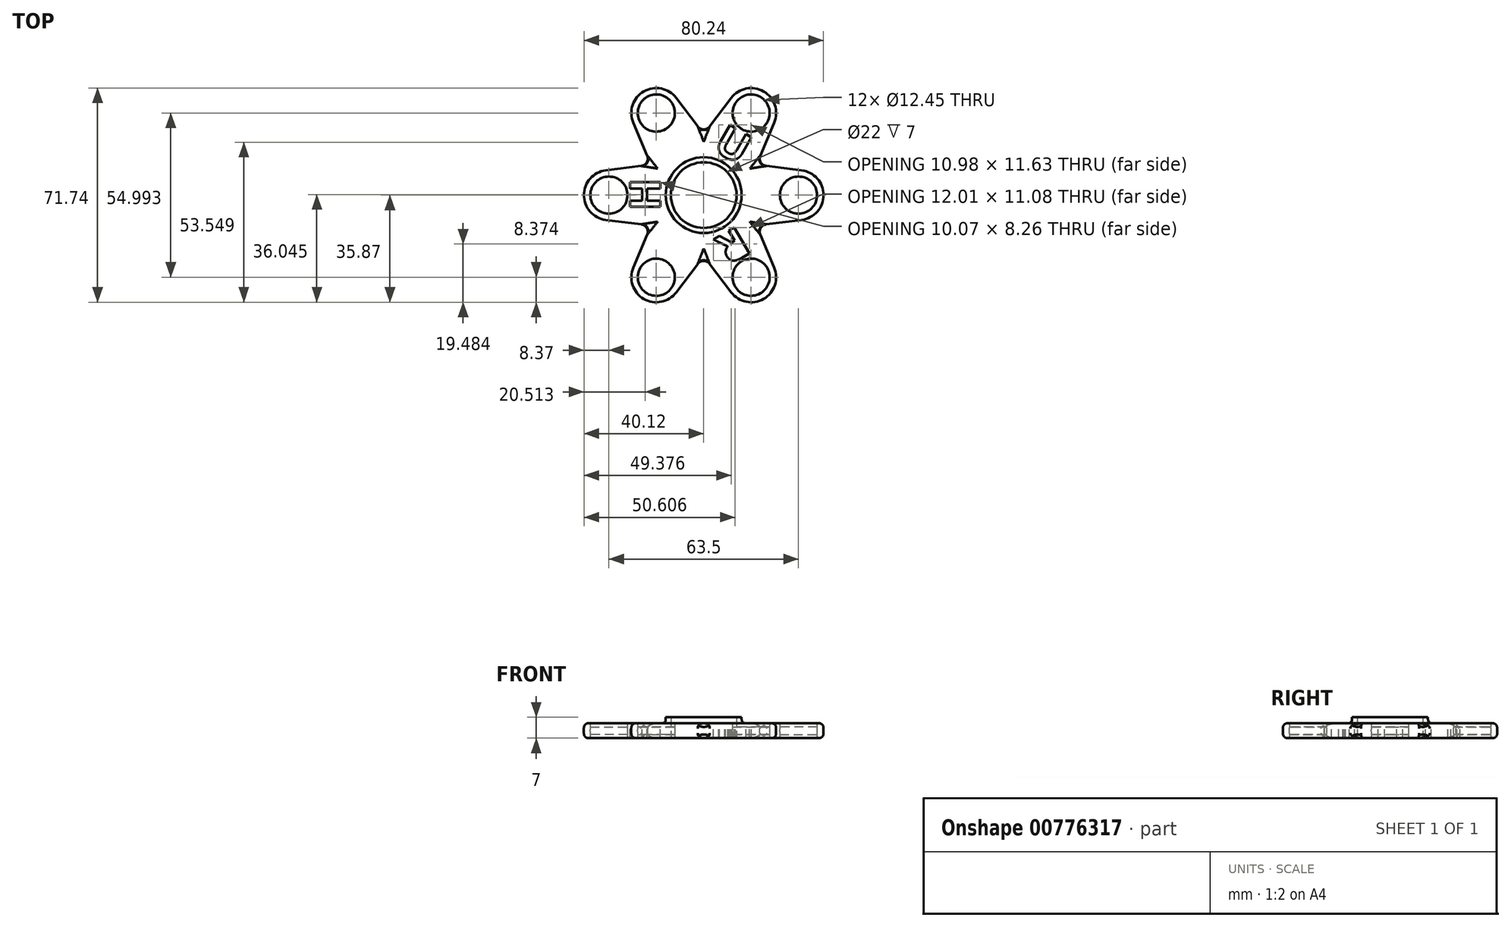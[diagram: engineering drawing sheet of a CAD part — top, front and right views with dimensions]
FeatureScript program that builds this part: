
annotation { "Feature Type Name" : "Feature", "Feature Type Description" : "" }
export const myFeature = defineFeature(function(context is Context, id is Id, definition is map)
    precondition{}
    {
        {
            var Q0;
            Q0=qCreatedBy(makeId("Top.planeOp"),FACE);
            var sketch = newSketch(context, id + "F0", { "sketchPlane" : qUnion([Q0])});
            skCircle(sketch, "E0", {"center": v(0, 0) * mm, "radius": 12.7 * mm});
            skCircle(sketch, "E1", {"center": v(0, 0) * mm, "radius": 11 * mm});
            skSolve(sketch);
        }
        {
            var Q0;
            Q0=makeQuery(id+"F0.imprint","IMPRINT",FACE,{"disambiguationData":[TD([[makeQuery(id+"F0.imprint","IMPRINT",EDGE,{"derivedFrom":sQuery(id+"F0.wireOp",EDGE,"E0")}),1.0]])]});
            extrude(context, id + "F1", {"entities" : qUnion([Q0]), "depth" : 7 * mm, "offsetDistance" : 25.4 * mm});
        }
        {
            var Q0;
            Q0=qCreatedBy(makeId("Top.planeOp"),FACE);
            cPlane(context, id + "F2", {"entities" : qUnion([Q0]), "cplaneType" : CPlaneType.OFFSET, "offset" : 2.5 * mm, "width" : 152.4 * mm, "height" : 152.4 * mm});
        }
        {
            var Q0;
            Q0=qCreatedBy(id+"F2.planeOp",FACE);
            var sketch = newSketch(context, id + "F3", { "sketchPlane" : qUnion([Q0])});
            skArc(sketch, "E2", {"start": v(-32.77, 8.31) * mm, "mid": v(-40.12, 0) * mm, "end": v(-32.77, -8.31) * mm});
            skLineSegment(sketch, "E3", {"start": v(-32.77, 8.31) * mm, "end": v(0, 12.35) * mm});
            skLineSegment(sketch, "E4.MirrorCS", {"start": v(-32.77, -8.31) * mm, "end": v(0, -12.35) * mm});
            skLineSegment(sketch, "E5", {"start": v(0, 12.35) * mm, "end": v(0, 11.32) * mm});
            skArc(sketch, "E6", {"start": v(0, 11.32) * mm, "mid": v(-11.32, 0) * mm, "end": v(0, -11.32) * mm});
            skLineSegment(sketch, "E7.trimOffspring", {"start": v(0, -11.32) * mm, "end": v(0, -12.35) * mm});
            skArc(sketch, "E8", {"start": v(-31.75, 6.35) * mm, "mid": v(-38.1, 0) * mm, "end": v(-31.75, -6.35) * mm});
            skLineSegment(sketch, "E9", {"start": v(-31.75, 6.35) * mm, "end": v(-31.75, -6.35) * mm});
            skCircle(sketch, "E10", {"center": v(-31.75, 0) * mm, "radius": 6.22 * mm});
            skSolve(sketch);
        }
        {
            var Q0;
            Q0=makeQuery(id+"F3.imprint","IMPRINT",FACE,{"disambiguationData":[TD([[makeQuery(id+"F3.imprint","IMPRINT",EDGE,{"derivedFrom":sQuery(id+"F3.wireOp",EDGE,"E2")}),1.0]])]});
            var Q1;
            {var subQ0=sQuery(id+"F3.wireOp",EDGE,"E8");Q1=makeQuery(id+"F3.imprint","IMPRINT",FACE,{"disambiguationData":[TD([[makeQuery(id+"F3.imprint","IMPRINT",EDGE,{"derivedFrom":subQ0}),1.0]])]});}
            extrude(context, id + "F4", {"entities" : qUnion([Q0, Q1]), "endBound" : BoundingType.SYMMETRIC, "depth" : 5 * mm, "offsetDistance" : 25.4 * mm});
        }
        {
            var Q0;
            Q0=qCreatedBy(makeId("Front.planeOp"),FACE);
            var sketch = newSketch(context, id + "F5", { "sketchPlane" : qUnion([Q0])});
            skLineSegment(sketch, "E11", {"start": v(0, 0) * mm, "end": v(0, 41) * mm, "construction": true});
            skSolve(sketch);
        }
        {
            var Q0;
            Q0=makeQuery(id+"F3.imprint","IMPRINT",FACE,{"disambiguationData":[TD([[makeQuery(id+"F3.imprint","IMPRINT",EDGE,{"derivedFrom":sQuery(id+"F3.wireOp",EDGE,"E8")}),1.0]])]});
            var Q1;
            Q1=sQuery(id+"F3.wireOp",EDGE,"E9");
            revolve(context, id + "F6", {"operationType" : NewBodyOperationType.REMOVE, "surfaceOperationType" : NewSurfaceOperationType.NEW, "entities" : qUnion([Q0]), "axis" : qUnion([Q1]), "revolveType" : RevolveType.FULL, "oppositeDirection" : true});
        }
        {
            var Q0;
            Q0=makeQuery(id+"F4.opExtrude","SWEPT_BODY",BODY,{"disambiguationData":[OSD([sQuery(id+"F3.wireOp",EDGE,"E2"),sQuery(id+"F3.wireOp",EDGE,"E3"),sQuery(id+"F3.wireOp",EDGE,"E4.MirrorCS"),sQuery(id+"F3.wireOp",EDGE,"E5"),sQuery(id+"F3.wireOp",EDGE,"gVdO0x3I-Yq7t-95zV-3Q7Q-V35kwEtAvBfn"),sQuery(id+"F3.wireOp",EDGE,"E6"),sQuery(id+"F3.wireOp",EDGE,"E7.trimOffspring")])]});
            var Q1;
            Q1=sQuery(id+"F5.wireOp",EDGE,"E11");
            circularPattern(context, id + "F7", {"entities" : qUnion([Q0]), "axis" : qUnion([Q1]), "angle" : 360 * degree, "instanceCount" : 6, "equalSpace" : true});
        }
        {
            var Q0;
            Q0=makeQuery(id+"F1.opExtrude","SWEPT_BODY",BODY,{"disambiguationData":[OSD([sQuery(id+"F0.wireOp",EDGE,"E0"),sQuery(id+"F0.wireOp",EDGE,"E1")])]});
            var Q1;
            Q1=makeQuery(id+"F4.opExtrude","SWEPT_BODY",BODY,{"disambiguationData":[OSD([sQuery(id+"F3.wireOp",EDGE,"E2"),sQuery(id+"F3.wireOp",EDGE,"E3"),sQuery(id+"F3.wireOp",EDGE,"E4.MirrorCS"),sQuery(id+"F3.wireOp",EDGE,"E5"),sQuery(id+"F3.wireOp",EDGE,"gVdO0x3I-Yq7t-95zV-3Q7Q-V35kwEtAvBfn"),sQuery(id+"F3.wireOp",EDGE,"E6"),sQuery(id+"F3.wireOp",EDGE,"E7.trimOffspring")])]});
            var Q2;
            Q2=makeQuery(id+"F7.opPattern","COPY",BODY,{"derivedFrom":makeQuery(id+"F4.opExtrude","SWEPT_BODY",BODY,{"disambiguationData":[OSD([sQuery(id+"F3.wireOp",EDGE,"E2"),sQuery(id+"F3.wireOp",EDGE,"E3"),sQuery(id+"F3.wireOp",EDGE,"E4.MirrorCS"),sQuery(id+"F3.wireOp",EDGE,"E5"),sQuery(id+"F3.wireOp",EDGE,"gVdO0x3I-Yq7t-95zV-3Q7Q-V35kwEtAvBfn"),sQuery(id+"F3.wireOp",EDGE,"E6"),sQuery(id+"F3.wireOp",EDGE,"E7.trimOffspring")])]}),"instanceName":"1"});
            var Q3;
            Q3=makeQuery(id+"F7.opPattern","COPY",BODY,{"derivedFrom":makeQuery(id+"F4.opExtrude","SWEPT_BODY",BODY,{"disambiguationData":[OSD([sQuery(id+"F3.wireOp",EDGE,"E2"),sQuery(id+"F3.wireOp",EDGE,"E3"),sQuery(id+"F3.wireOp",EDGE,"E4.MirrorCS"),sQuery(id+"F3.wireOp",EDGE,"E5"),sQuery(id+"F3.wireOp",EDGE,"gVdO0x3I-Yq7t-95zV-3Q7Q-V35kwEtAvBfn"),sQuery(id+"F3.wireOp",EDGE,"E6"),sQuery(id+"F3.wireOp",EDGE,"E7.trimOffspring")])]}),"instanceName":"2"});
            var Q4;
            Q4=makeQuery(id+"F7.opPattern","COPY",BODY,{"derivedFrom":makeQuery(id+"F4.opExtrude","SWEPT_BODY",BODY,{"disambiguationData":[OSD([sQuery(id+"F3.wireOp",EDGE,"E2"),sQuery(id+"F3.wireOp",EDGE,"E3"),sQuery(id+"F3.wireOp",EDGE,"E4.MirrorCS"),sQuery(id+"F3.wireOp",EDGE,"E5"),sQuery(id+"F3.wireOp",EDGE,"gVdO0x3I-Yq7t-95zV-3Q7Q-V35kwEtAvBfn"),sQuery(id+"F3.wireOp",EDGE,"E6"),sQuery(id+"F3.wireOp",EDGE,"E7.trimOffspring")])]}),"instanceName":"3"});
            var Q5;
            Q5=makeQuery(id+"F7.opPattern","COPY",BODY,{"derivedFrom":makeQuery(id+"F4.opExtrude","SWEPT_BODY",BODY,{"disambiguationData":[OSD([sQuery(id+"F3.wireOp",EDGE,"E2"),sQuery(id+"F3.wireOp",EDGE,"E3"),sQuery(id+"F3.wireOp",EDGE,"E4.MirrorCS"),sQuery(id+"F3.wireOp",EDGE,"E5"),sQuery(id+"F3.wireOp",EDGE,"gVdO0x3I-Yq7t-95zV-3Q7Q-V35kwEtAvBfn"),sQuery(id+"F3.wireOp",EDGE,"E6"),sQuery(id+"F3.wireOp",EDGE,"E7.trimOffspring")])]}),"instanceName":"4"});
            var Q6;
            Q6=makeQuery(id+"F7.opPattern","COPY",BODY,{"derivedFrom":makeQuery(id+"F4.opExtrude","SWEPT_BODY",BODY,{"disambiguationData":[OSD([sQuery(id+"F3.wireOp",EDGE,"E2"),sQuery(id+"F3.wireOp",EDGE,"E3"),sQuery(id+"F3.wireOp",EDGE,"E4.MirrorCS"),sQuery(id+"F3.wireOp",EDGE,"E5"),sQuery(id+"F3.wireOp",EDGE,"gVdO0x3I-Yq7t-95zV-3Q7Q-V35kwEtAvBfn"),sQuery(id+"F3.wireOp",EDGE,"E6"),sQuery(id+"F3.wireOp",EDGE,"E7.trimOffspring")])]}),"instanceName":"5"});
            booleanBodies(context, id + "F8", {"operationType" : BooleanOperationType.UNION, "tools" : qUnion([Q0, Q1, Q2, Q3, Q4, Q5, Q6])});
        }
        {
            var Q0;
            Q0=makeQuery(id+"F8.opBoolean","INTERSECT",EDGE,{"derivedFrom":[makeQuery(id+"F1.opExtrude","SWEPT_FACE",FACE,{"disambiguationData":[OSD([sQuery(id+"F0.wireOp",EDGE,"E0")])]}),makeQuery(id+"F7.opPattern","COPY",FACE,{"derivedFrom":makeQuery(id+"F4.opExtrude","CAP_FACE",FACE,{"disambiguationData":[OSD([sQuery(id+"F3.wireOp",EDGE,"E2"),sQuery(id+"F3.wireOp",EDGE,"E3"),sQuery(id+"F3.wireOp",EDGE,"E4.MirrorCS"),sQuery(id+"F3.wireOp",EDGE,"E5"),sQuery(id+"F3.wireOp",EDGE,"gVdO0x3I-Yq7t-95zV-3Q7Q-V35kwEtAvBfn"),sQuery(id+"F3.wireOp",EDGE,"E6"),sQuery(id+"F3.wireOp",EDGE,"E7.trimOffspring")])],"isStart":false}),"instanceName":"1"})]});
            var Q1;
            Q1=makeQuery(id+"F8.opBoolean","INTERSECT",EDGE,{"derivedFrom":[makeQuery(id+"F1.opExtrude","SWEPT_FACE",FACE,{"disambiguationData":[OSD([sQuery(id+"F0.wireOp",EDGE,"E0")])]}),makeQuery(id+"F7.opPattern","COPY",FACE,{"derivedFrom":makeQuery(id+"F4.opExtrude","CAP_FACE",FACE,{"disambiguationData":[OSD([sQuery(id+"F3.wireOp",EDGE,"E2"),sQuery(id+"F3.wireOp",EDGE,"E3"),sQuery(id+"F3.wireOp",EDGE,"E4.MirrorCS"),sQuery(id+"F3.wireOp",EDGE,"E5"),sQuery(id+"F3.wireOp",EDGE,"gVdO0x3I-Yq7t-95zV-3Q7Q-V35kwEtAvBfn"),sQuery(id+"F3.wireOp",EDGE,"E6"),sQuery(id+"F3.wireOp",EDGE,"E7.trimOffspring")])],"isStart":true}),"instanceName":"1"})]});
            fillet(context, id + "F9", {"entities" : qUnion([Q0, Q1]), "radius" : 1.27 * mm, "tangentPropagation" : true, "allowEdgeOverflow" : false});
        }
        {
            var Q0;
            Q0=makeQuery(id+"F4.opExtrude","CAP_EDGE",EDGE,{"disambiguationData":[OSD([sQuery(id+"F3.wireOp",EDGE,"E4.MirrorCS")])],"isStart":false});
            var Q1;
            Q1=makeQuery(id+"F7.opPattern","COPY",EDGE,{"derivedFrom":makeQuery(id+"F4.opExtrude","CAP_EDGE",EDGE,{"disambiguationData":[OSD([sQuery(id+"F3.wireOp",EDGE,"E3")])],"isStart":false}),"instanceName":"1"});
            var Q2;
            Q2=makeQuery(id+"F7.opPattern","COPY",EDGE,{"derivedFrom":makeQuery(id+"F4.opExtrude","CAP_EDGE",EDGE,{"disambiguationData":[OSD([sQuery(id+"F3.wireOp",EDGE,"E2")])],"isStart":false}),"instanceName":"1"});
            var Q3;
            Q3=makeQuery(id+"F7.opPattern","COPY",EDGE,{"derivedFrom":makeQuery(id+"F4.opExtrude","CAP_EDGE",EDGE,{"disambiguationData":[OSD([sQuery(id+"F3.wireOp",EDGE,"E4.MirrorCS")])],"isStart":false}),"instanceName":"1"});
            var Q4;
            Q4=makeQuery(id+"F7.opPattern","COPY",EDGE,{"derivedFrom":makeQuery(id+"F4.opExtrude","CAP_EDGE",EDGE,{"disambiguationData":[OSD([sQuery(id+"F3.wireOp",EDGE,"E3")])],"isStart":false}),"instanceName":"2"});
            var Q5;
            Q5=makeQuery(id+"F7.opPattern","COPY",EDGE,{"derivedFrom":makeQuery(id+"F4.opExtrude","CAP_EDGE",EDGE,{"disambiguationData":[OSD([sQuery(id+"F3.wireOp",EDGE,"E2")])],"isStart":false}),"instanceName":"2"});
            var Q6;
            Q6=makeQuery(id+"F7.opPattern","COPY",EDGE,{"derivedFrom":makeQuery(id+"F4.opExtrude","CAP_EDGE",EDGE,{"disambiguationData":[OSD([sQuery(id+"F3.wireOp",EDGE,"E4.MirrorCS")])],"isStart":false}),"instanceName":"2"});
            var Q7;
            Q7=makeQuery(id+"F7.opPattern","COPY",EDGE,{"derivedFrom":makeQuery(id+"F4.opExtrude","CAP_EDGE",EDGE,{"disambiguationData":[OSD([sQuery(id+"F3.wireOp",EDGE,"E3")])],"isStart":false}),"instanceName":"3"});
            var Q8;
            Q8=makeQuery(id+"F7.opPattern","COPY",EDGE,{"derivedFrom":makeQuery(id+"F4.opExtrude","CAP_EDGE",EDGE,{"disambiguationData":[OSD([sQuery(id+"F3.wireOp",EDGE,"E2")])],"isStart":false}),"instanceName":"3"});
            var Q9;
            Q9=makeQuery(id+"F7.opPattern","COPY",EDGE,{"derivedFrom":makeQuery(id+"F4.opExtrude","CAP_EDGE",EDGE,{"disambiguationData":[OSD([sQuery(id+"F3.wireOp",EDGE,"E4.MirrorCS")])],"isStart":false}),"instanceName":"3"});
            var Q10;
            Q10=makeQuery(id+"F7.opPattern","COPY",EDGE,{"derivedFrom":makeQuery(id+"F4.opExtrude","CAP_EDGE",EDGE,{"disambiguationData":[OSD([sQuery(id+"F3.wireOp",EDGE,"E3")])],"isStart":false}),"instanceName":"4"});
            var Q11;
            Q11=makeQuery(id+"F7.opPattern","COPY",EDGE,{"derivedFrom":makeQuery(id+"F4.opExtrude","CAP_EDGE",EDGE,{"disambiguationData":[OSD([sQuery(id+"F3.wireOp",EDGE,"E4.MirrorCS")])],"isStart":false}),"instanceName":"4"});
            var Q12;
            Q12=makeQuery(id+"F7.opPattern","COPY",EDGE,{"derivedFrom":makeQuery(id+"F4.opExtrude","CAP_EDGE",EDGE,{"disambiguationData":[OSD([sQuery(id+"F3.wireOp",EDGE,"E2")])],"isStart":false}),"instanceName":"4"});
            var Q13;
            Q13=makeQuery(id+"F7.opPattern","COPY",EDGE,{"derivedFrom":makeQuery(id+"F4.opExtrude","CAP_EDGE",EDGE,{"disambiguationData":[OSD([sQuery(id+"F3.wireOp",EDGE,"E3")])],"isStart":false}),"instanceName":"5"});
            var Q14;
            Q14=makeQuery(id+"F7.opPattern","COPY",EDGE,{"derivedFrom":makeQuery(id+"F4.opExtrude","CAP_EDGE",EDGE,{"disambiguationData":[OSD([sQuery(id+"F3.wireOp",EDGE,"E4.MirrorCS")])],"isStart":false}),"instanceName":"5"});
            var Q15;
            Q15=makeQuery(id+"F7.opPattern","COPY",EDGE,{"derivedFrom":makeQuery(id+"F4.opExtrude","CAP_EDGE",EDGE,{"disambiguationData":[OSD([sQuery(id+"F3.wireOp",EDGE,"E2")])],"isStart":false}),"instanceName":"5"});
            var Q16;
            Q16=makeQuery(id+"F4.opExtrude","CAP_EDGE",EDGE,{"disambiguationData":[OSD([sQuery(id+"F3.wireOp",EDGE,"E3")])],"isStart":false});
            var Q17;
            Q17=makeQuery(id+"F4.opExtrude","CAP_EDGE",EDGE,{"disambiguationData":[OSD([sQuery(id+"F3.wireOp",EDGE,"E2")])],"isStart":false});
            var Q18;
            Q18=makeQuery(id+"F4.opExtrude","CAP_EDGE",EDGE,{"disambiguationData":[OSD([sQuery(id+"F3.wireOp",EDGE,"E4.MirrorCS")])],"isStart":true});
            var Q19;
            Q19=makeQuery(id+"F7.opPattern","COPY",EDGE,{"derivedFrom":makeQuery(id+"F4.opExtrude","CAP_EDGE",EDGE,{"disambiguationData":[OSD([sQuery(id+"F3.wireOp",EDGE,"E3")])],"isStart":true}),"instanceName":"1"});
            var Q20;
            Q20=makeQuery(id+"F7.opPattern","COPY",EDGE,{"derivedFrom":makeQuery(id+"F4.opExtrude","CAP_EDGE",EDGE,{"disambiguationData":[OSD([sQuery(id+"F3.wireOp",EDGE,"E3")])],"isStart":true}),"instanceName":"2"});
            var Q21;
            Q21=makeQuery(id+"F7.opPattern","COPY",EDGE,{"derivedFrom":makeQuery(id+"F4.opExtrude","CAP_EDGE",EDGE,{"disambiguationData":[OSD([sQuery(id+"F3.wireOp",EDGE,"E3")])],"isStart":true}),"instanceName":"3"});
            var Q22;
            Q22=makeQuery(id+"F7.opPattern","COPY",EDGE,{"derivedFrom":makeQuery(id+"F4.opExtrude","CAP_EDGE",EDGE,{"disambiguationData":[OSD([sQuery(id+"F3.wireOp",EDGE,"E3")])],"isStart":true}),"instanceName":"4"});
            var Q23;
            Q23=makeQuery(id+"F7.opPattern","COPY",EDGE,{"derivedFrom":makeQuery(id+"F4.opExtrude","CAP_EDGE",EDGE,{"disambiguationData":[OSD([sQuery(id+"F3.wireOp",EDGE,"E3")])],"isStart":true}),"instanceName":"5"});
            fillet(context, id + "F10", {"entities" : qUnion([Q0, Q1, Q2, Q3, Q4, Q5, Q6, Q7, Q8, Q9, Q10, Q11, Q12, Q13, Q14, Q15, Q16, Q17, Q18, Q19, Q20, Q21, Q22, Q23]), "radius" : 1.52 * mm, "tangentPropagation" : true, "allowEdgeOverflow" : false});
        }
        {
            var Q0;
            Q0=makeQuery(id+"F8.opBoolean","INTERSECT",EDGE,{"derivedFrom":[makeQuery(id+"F4.opExtrude","SWEPT_FACE",FACE,{"disambiguationData":[OSD([sQuery(id+"F3.wireOp",EDGE,"E4.MirrorCS")])]}),makeQuery(id+"F7.opPattern","COPY",FACE,{"derivedFrom":makeQuery(id+"F4.opExtrude","SWEPT_FACE",FACE,{"disambiguationData":[OSD([sQuery(id+"F3.wireOp",EDGE,"E3")])]}),"instanceName":"1"})]});
            var Q1;
            Q1=makeQuery(id+"F10.opFillet","BLEND_EDGE",EDGE,{"blendedFrom":[makeQuery(id+"F7.opPattern","COPY",EDGE,{"derivedFrom":makeQuery(id+"F4.opExtrude","CAP_EDGE",EDGE,{"disambiguationData":[OSD([sQuery(id+"F3.wireOp",EDGE,"E4.MirrorCS")])],"isStart":false}),"instanceName":"1"}),makeQuery(id+"F7.opPattern","COPY",EDGE,{"derivedFrom":makeQuery(id+"F4.opExtrude","CAP_EDGE",EDGE,{"disambiguationData":[OSD([sQuery(id+"F3.wireOp",EDGE,"E3")])],"isStart":false}),"instanceName":"2"})],"blendedInto":[]});
            var Q2;
            Q2=makeQuery(id+"F10.opFillet","BLEND_EDGE",EDGE,{"blendedFrom":[makeQuery(id+"F7.opPattern","COPY",EDGE,{"derivedFrom":makeQuery(id+"F4.opExtrude","CAP_EDGE",EDGE,{"disambiguationData":[OSD([sQuery(id+"F3.wireOp",EDGE,"E4.MirrorCS")])],"isStart":false}),"instanceName":"2"}),makeQuery(id+"F7.opPattern","COPY",EDGE,{"derivedFrom":makeQuery(id+"F4.opExtrude","CAP_EDGE",EDGE,{"disambiguationData":[OSD([sQuery(id+"F3.wireOp",EDGE,"E3")])],"isStart":false}),"instanceName":"3"})],"blendedInto":[]});
            var Q3;
            Q3=makeQuery(id+"F10.opFillet","BLEND_EDGE",EDGE,{"blendedFrom":[makeQuery(id+"F4.opExtrude","CAP_EDGE",EDGE,{"disambiguationData":[OSD([sQuery(id+"F3.wireOp",EDGE,"E3")])],"isStart":false}),makeQuery(id+"F7.opPattern","COPY",EDGE,{"derivedFrom":makeQuery(id+"F4.opExtrude","CAP_EDGE",EDGE,{"disambiguationData":[OSD([sQuery(id+"F3.wireOp",EDGE,"E4.MirrorCS")])],"isStart":false}),"instanceName":"5"})],"blendedInto":[]});
            var Q4;
            Q4=makeQuery(id+"F10.opFillet","BLEND_EDGE",EDGE,{"blendedFrom":[makeQuery(id+"F7.opPattern","COPY",EDGE,{"derivedFrom":makeQuery(id+"F4.opExtrude","CAP_EDGE",EDGE,{"disambiguationData":[OSD([sQuery(id+"F3.wireOp",EDGE,"E4.MirrorCS")])],"isStart":false}),"instanceName":"4"}),makeQuery(id+"F7.opPattern","COPY",EDGE,{"derivedFrom":makeQuery(id+"F4.opExtrude","CAP_EDGE",EDGE,{"disambiguationData":[OSD([sQuery(id+"F3.wireOp",EDGE,"E3")])],"isStart":false}),"instanceName":"5"})],"blendedInto":[]});
            var Q5;
            Q5=makeQuery(id+"F10.opFillet","BLEND_EDGE",EDGE,{"blendedFrom":[makeQuery(id+"F7.opPattern","COPY",EDGE,{"derivedFrom":makeQuery(id+"F4.opExtrude","CAP_EDGE",EDGE,{"disambiguationData":[OSD([sQuery(id+"F3.wireOp",EDGE,"E4.MirrorCS")])],"isStart":false}),"instanceName":"3"}),makeQuery(id+"F7.opPattern","COPY",EDGE,{"derivedFrom":makeQuery(id+"F4.opExtrude","CAP_EDGE",EDGE,{"disambiguationData":[OSD([sQuery(id+"F3.wireOp",EDGE,"E3")])],"isStart":false}),"instanceName":"4"})],"blendedInto":[]});
            fillet(context, id + "F11", {"entities" : qUnion([Q0, Q1, Q2, Q3, Q4, Q5]), "radius" : 2.54 * mm, "tangentPropagation" : true, "allowEdgeOverflow" : false});
        }
        {
            var Q0;
            Q0=qCreatedBy(makeId("Top.planeOp"),FACE);
            var sketch = newSketch(context, id + "F12", { "sketchPlane" : qUnion([Q0])});
            skText(sketch, "E12", { "text": "H", "fontName": "OpenSans-Bold.ttf"});
            skText(sketch, "E13", { "text": "U", "fontName": "OpenSans-Bold.ttf"});
            skText(sketch, "E14", { "text": "R", "fontName": "OpenSans-Bold.ttf"});
            const initialGuessF12  = {"E12": [-0.01457, -0.00522, 0, 1, 0.01016], "E13": [0.00274, 0.01537, 0.86603, -0.5, 0.01016], "E14": [0.01132, -0.01021, -0.86603, -0.5, 0.01016]};
            skSetInitialGuess(sketch, initialGuessF12);
            skSolve(sketch);
        }
        {
            var Q0;
            Q0=qSketchRegion(id+"F12",true);
            extrude(context, id + "F13", {"entities" : qUnion([Q0]), "operationType" : NewBodyOperationType.REMOVE, "endBound" : BoundingType.SYMMETRIC, "oppositeDirection" : true, "depth" : 25.4 * mm, "offsetDistance" : 25.4 * mm});
        }
        {
            var Q0;
            Q0=qCreatedBy(makeId("Top.planeOp"),FACE);
            var sketch = newSketch(context, id + "F14", { "sketchPlane" : qUnion([Q0])});
            skCircle(sketch, "E15", {"center": v(10.87, -18.55) * mm, "radius": 2.27 * mm});
            skSolve(sketch);
        }
        {
            var Q0;
            Q0=qSketchRegion(id+"F14",true);
            extrude(context, id + "F15", {"entities" : qUnion([Q0]), "operationType" : NewBodyOperationType.REMOVE, "endBound" : BoundingType.SYMMETRIC, "oppositeDirection" : true, "depth" : 25.4 * mm, "offsetDistance" : 25.4 * mm});
        }
    });
